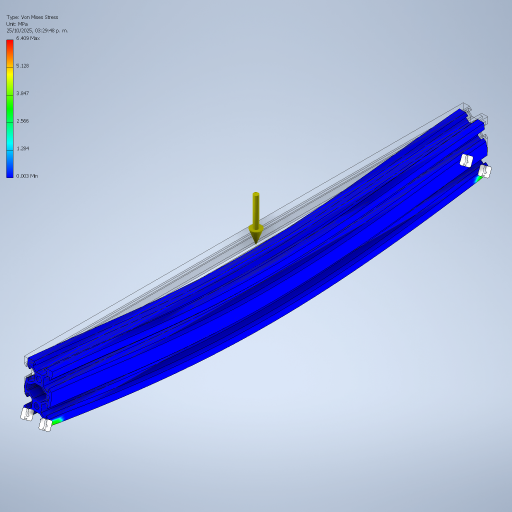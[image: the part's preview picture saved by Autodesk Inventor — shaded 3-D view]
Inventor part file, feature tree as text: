
AUTODESK INVENTOR PART (.ipt)
format: ipt  version: 2024.2 (Build 282272000, 272)  size: 523,264 bytes
history: native  units: mm
features: extrude x2, sketch x2, pattern_linear x1
ambient origin geometry x8: Origin, YZ Plane, XZ Plane, XY Plane, X Axis, Y Axis, Z Axis, Center Point
bodies: Solid1 (feature_tree)
feature tree (5):
  extrude  "Extrusion1"  Depth=10.0mm
  pattern_linear  "Rectangular Pattern1"  Spacing1=4.4mm  [1 undecoded]
  extrude  "Extrusion2"  TaperAngle=45.0deg  [1 undecoded]
  sketch  "Sketch1"  dims[d16=10.0mm d19=3.2mm]
  sketch  "Sketch2"  dims[d21=4.4mm d22=4.4mm d24=45.0deg d25=1.8mm d27=1.8mm d28=45.0deg d29=3.2mm d31=1.4mm d33=2.15mm d34=3.825mm d35=3.825mm d36=135.0deg d37=40.0mm d39=360.0deg d41=360.0mm d42=0.0mm d43=20.0mm d45=20.0mm d46=4.5mm d48=400.0mm d49=0.0mm d50=1.8mm d51=0.5mm d52=0.872665mm d53=0.5mm d54=0.872665mm]
note: 2 required parameter values undecoded (feature->parameter linkage not recoverable at this tier; creation-order binding heuristic only, values carry confidence <= 0.55)
